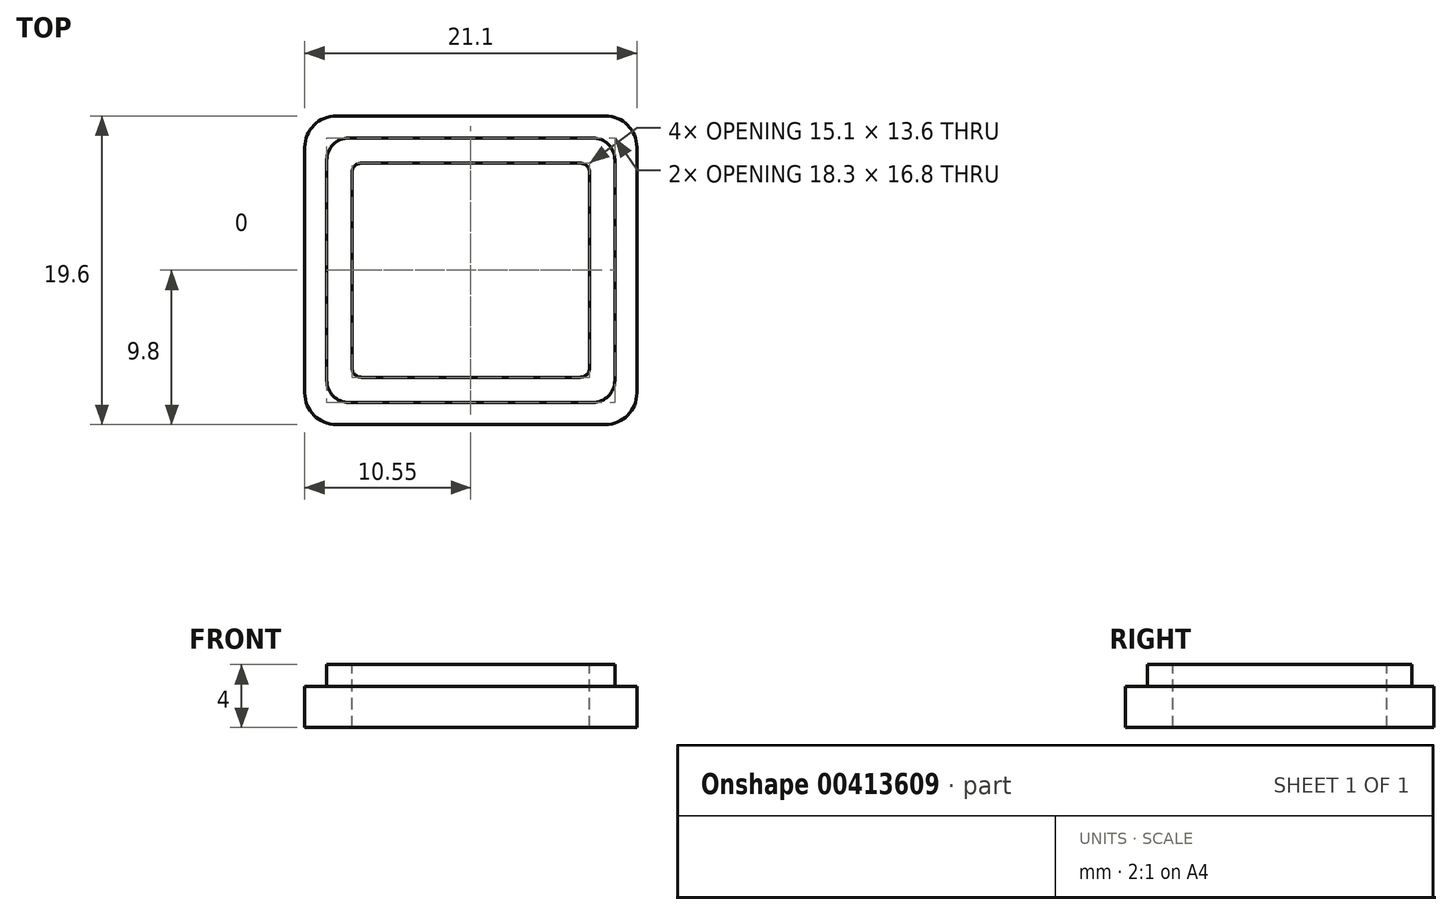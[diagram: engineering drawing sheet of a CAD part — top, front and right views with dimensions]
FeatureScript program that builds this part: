
annotation { "Feature Type Name" : "Feature", "Feature Type Description" : "" }
export const myFeature = defineFeature(function(context is Context, id is Id, definition is map)
    precondition{}
    {
        {
            var Q0;
            Q0=qCreatedBy(makeId("Top.planeOp"),FACE);
            var sketch = newSketch(context, id + "F0", { "sketchPlane" : qUnion([Q0])});
            skLineSegment(sketch, "E0.bottom", {"start": v(0, 0) * mm, "end": v(21.1, 0) * mm});
            skLineSegment(sketch, "E0.top", {"start": v(0, 19.6) * mm, "end": v(21.1, 19.6) * mm});
            skLineSegment(sketch, "E0.left", {"start": v(0, 0) * mm, "end": v(0, 19.6) * mm});
            skLineSegment(sketch, "E0.right", {"start": v(21.1, 0) * mm, "end": v(21.1, 19.6) * mm});
            skSolve(sketch);
        }
        {
            var Q0;
            Q0 = qSketchRegion(id + "F0", true);
            extrude(context, id + "F1", {"entities" : qUnion([Q0]), "depth" : 4 * mm, "offsetDistance" : 25 * mm});
        }
        {
            var Q0;
            Q0=makeQuery(id+"F1.opExtrude","CAP_FACE",FACE,{"disambiguationData":[OSD([sQuery(id+"F0.wireOp",EDGE,"E0.bottom"),sQuery(id+"F0.wireOp",EDGE,"E0.top"),sQuery(id+"F0.wireOp",EDGE,"E0.left"),sQuery(id+"F0.wireOp",EDGE,"E0.right")])],"isStart":false});
            var sketch = newSketch(context, id + "F2", { "sketchPlane" : qUnion([Q0])});
            skLineSegment(sketch, "E1.bottom", {"start": v(1.4, 18.2) * mm, "end": v(19.7, 18.2) * mm});
            skLineSegment(sketch, "E1.top", {"start": v(1.4, 1.4) * mm, "end": v(19.7, 1.4) * mm});
            skLineSegment(sketch, "E1.left", {"start": v(1.4, 18.2) * mm, "end": v(1.4, 1.4) * mm});
            skLineSegment(sketch, "E1.right", {"start": v(19.7, 18.2) * mm, "end": v(19.7, 1.4) * mm});
            skLineSegment(sketch, "E2.bottom", {"start": v(0, 19.6) * mm, "end": v(21.1, 19.6) * mm});
            skLineSegment(sketch, "E2.top", {"start": v(0, 0) * mm, "end": v(21.1, 0) * mm});
            skLineSegment(sketch, "E2.left", {"start": v(0, 19.6) * mm, "end": v(0, 0) * mm});
            skLineSegment(sketch, "E2.right", {"start": v(21.1, 19.6) * mm, "end": v(21.1, 0) * mm});
            skSolve(sketch);
        }
        {
            var Q0;
            Q0 = qSketchRegion(id + "F2", true);
            extrude(context, id + "F3", {"entities" : qUnion([Q0]), "operationType" : NewBodyOperationType.REMOVE, "oppositeDirection" : true, "depth" : 1.4 * mm, "offsetDistance" : 25 * mm});
        }
        {
            var Q0;
            Q0=makeQuery(id+"F1.opExtrude","CAP_FACE",FACE,{"disambiguationData":[OSD([sQuery(id+"F0.wireOp",EDGE,"E0.bottom"),sQuery(id+"F0.wireOp",EDGE,"E0.top"),sQuery(id+"F0.wireOp",EDGE,"E0.left"),sQuery(id+"F0.wireOp",EDGE,"E0.right")])],"isStart":false});
            var sketch = newSketch(context, id + "F4", { "sketchPlane" : qUnion([Q0])});
            skLineSegment(sketch, "E3.bottom", {"start": v(3, 16.6) * mm, "end": v(18.1, 16.6) * mm});
            skLineSegment(sketch, "E3.top", {"start": v(3, 3) * mm, "end": v(18.1, 3) * mm});
            skLineSegment(sketch, "E3.left", {"start": v(3, 16.6) * mm, "end": v(3, 3) * mm});
            skLineSegment(sketch, "E3.right", {"start": v(18.1, 16.6) * mm, "end": v(18.1, 3) * mm});
            skSolve(sketch);
        }
        {
            var Q0;
            Q0 = qSketchRegion(id + "F4", true);
            extrude(context, id + "F5", {"entities" : qUnion([Q0]), "operationType" : NewBodyOperationType.REMOVE, "oppositeDirection" : true, "depth" : 25 * mm, "offsetDistance" : 25 * mm});
        }
        {
            var Q0;
            Q0=makeQuery(id+"F1.opExtrude","SWEPT_EDGE",EDGE,{"disambiguationData":[OSD([sQuery(id+"F0.wireOp",EDGE,"E0.top"),sQuery(id+"F0.wireOp",EDGE,"E0.right")])]});
            var Q1;
            Q1=makeQuery(id+"F1.opExtrude","SWEPT_EDGE",EDGE,{"disambiguationData":[OSD([sQuery(id+"F0.wireOp",EDGE,"E0.bottom"),sQuery(id+"F0.wireOp",EDGE,"E0.right")])]});
            var Q2;
            Q2=makeQuery(id+"F1.opExtrude","SWEPT_EDGE",EDGE,{"disambiguationData":[OSD([sQuery(id+"F0.wireOp",EDGE,"E0.bottom"),sQuery(id+"F0.wireOp",EDGE,"E0.left")])]});
            var Q3;
            Q3=makeQuery(id+"F1.opExtrude","SWEPT_EDGE",EDGE,{"disambiguationData":[OSD([sQuery(id+"F0.wireOp",EDGE,"E0.top"),sQuery(id+"F0.wireOp",EDGE,"E0.left")])]});
            fillet(context, id + "F6", {"entities" : qUnion([Q0, Q1, Q2, Q3]), "radius" : 2 * mm, "tangentPropagation" : true, "allowEdgeOverflow" : false});
        }
        {
            var Q0;
            Q0=makeQuery(id+"F5.boolean.opBoolean","COPY",EDGE,{"derivedFrom":makeQuery(id+"F5.opExtrude","SWEPT_EDGE",EDGE,{"disambiguationData":[OSD([sQuery(id+"F4.wireOp",EDGE,"E3.bottom"),sQuery(id+"F4.wireOp",EDGE,"E3.left")])]})});
            var Q1;
            Q1=makeQuery(id+"F5.boolean.opBoolean","COPY",EDGE,{"derivedFrom":makeQuery(id+"F5.opExtrude","SWEPT_EDGE",EDGE,{"disambiguationData":[OSD([sQuery(id+"F4.wireOp",EDGE,"E3.bottom"),sQuery(id+"F4.wireOp",EDGE,"E3.right")])]})});
            var Q2;
            Q2=makeQuery(id+"F5.boolean.opBoolean","COPY",EDGE,{"derivedFrom":makeQuery(id+"F5.opExtrude","SWEPT_EDGE",EDGE,{"disambiguationData":[OSD([sQuery(id+"F4.wireOp",EDGE,"E3.top"),sQuery(id+"F4.wireOp",EDGE,"E3.right")])]})});
            var Q3;
            Q3=makeQuery(id+"F5.boolean.opBoolean","COPY",EDGE,{"derivedFrom":makeQuery(id+"F5.opExtrude","SWEPT_EDGE",EDGE,{"disambiguationData":[OSD([sQuery(id+"F4.wireOp",EDGE,"E3.top"),sQuery(id+"F4.wireOp",EDGE,"E3.left")])]})});
            fillet(context, id + "F7", {"entities" : qUnion([Q0, Q1, Q2, Q3]), "radius" : 0.6 * mm, "tangentPropagation" : true, "allowEdgeOverflow" : false});
        }
        {
            var Q0;
            Q0=makeQuery(id+"F3.boolean.opBoolean","COPY",EDGE,{"derivedFrom":makeQuery(id+"F3.opExtrude","SWEPT_EDGE",EDGE,{"disambiguationData":[OSD([sQuery(id+"F2.wireOp",EDGE,"E1.top"),sQuery(id+"F2.wireOp",EDGE,"E1.left")])]})});
            var Q1;
            Q1=makeQuery(id+"F3.boolean.opBoolean","COPY",EDGE,{"derivedFrom":makeQuery(id+"F3.opExtrude","SWEPT_EDGE",EDGE,{"disambiguationData":[OSD([sQuery(id+"F2.wireOp",EDGE,"E1.top"),sQuery(id+"F2.wireOp",EDGE,"E1.right")])]})});
            var Q2;
            Q2=makeQuery(id+"F3.boolean.opBoolean","COPY",EDGE,{"derivedFrom":makeQuery(id+"F3.opExtrude","SWEPT_EDGE",EDGE,{"disambiguationData":[OSD([sQuery(id+"F2.wireOp",EDGE,"E1.bottom"),sQuery(id+"F2.wireOp",EDGE,"E1.right")])]})});
            var Q3;
            Q3=makeQuery(id+"F3.boolean.opBoolean","COPY",EDGE,{"derivedFrom":makeQuery(id+"F3.opExtrude","SWEPT_EDGE",EDGE,{"disambiguationData":[OSD([sQuery(id+"F2.wireOp",EDGE,"E1.bottom"),sQuery(id+"F2.wireOp",EDGE,"E1.left")])]})});
            fillet(context, id + "F8", {"entities" : qUnion([Q0, Q1, Q2, Q3]), "radius" : 1.4 * mm, "tangentPropagation" : true, "allowEdgeOverflow" : false});
        }
    });
